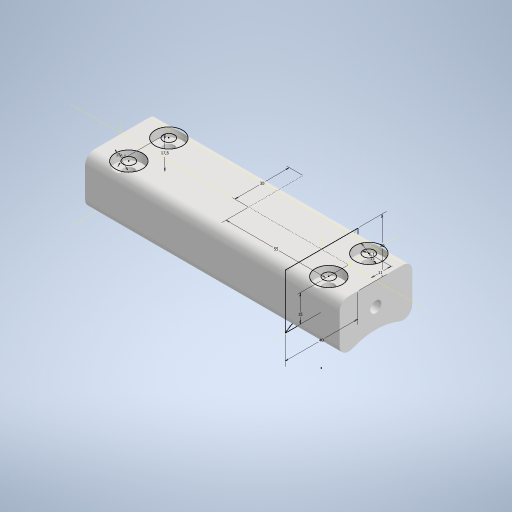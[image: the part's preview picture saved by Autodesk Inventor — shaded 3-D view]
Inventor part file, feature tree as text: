
AUTODESK INVENTOR PART (.ipt)
format: ipt  version: 2024.2 (Build 282272000, 272)  size: 344,576 bytes
history: native  units: mm
features: extrude x7, sketch x5, other x1, fillet x1, hole x1
ambient origin geometry x8: Origin, YZ Plane, XZ Plane, XY Plane, X Axis, Y Axis, Z Axis, Center Point
bodies: Body1 (feature_tree)
feature tree (15):
  other  "Bryła1"
  extrude  "Wyciągnięcie proste1"  Depth=30.0mm
  sketch  "Szkic2"
  extrude  "Wyciągnięcie proste2"  Depth=40.0mm
  extrude  "Wyciągnięcie proste3"  Depth=30.0mm TaperAngle=0.0deg
  fillet  "Zaokrąglenie1"  Radius=40.0mm
  sketch  "Szkic3"
  extrude  "Wyciągnięcie proste4"  Depth=30.0mm
  extrude  "Wyciągnięcie proste5"  Depth=15.0mm
  extrude  "Wyciągnięcie proste6"  Depth=110.0mm TaperAngle=0.0deg
  sketch  "Szkic5"
  sketch  "Szkic6"
  extrude  "Wyciągnięcie proste7"  TaperAngle=0.0deg  [1 undecoded]
  hole  "Otwór1"  [1 undecoded]
  sketch  "Szkic1"
note: 2 required parameter values undecoded (feature->parameter linkage not recoverable at this tier; creation-order binding heuristic only, values carry confidence <= 0.55)
